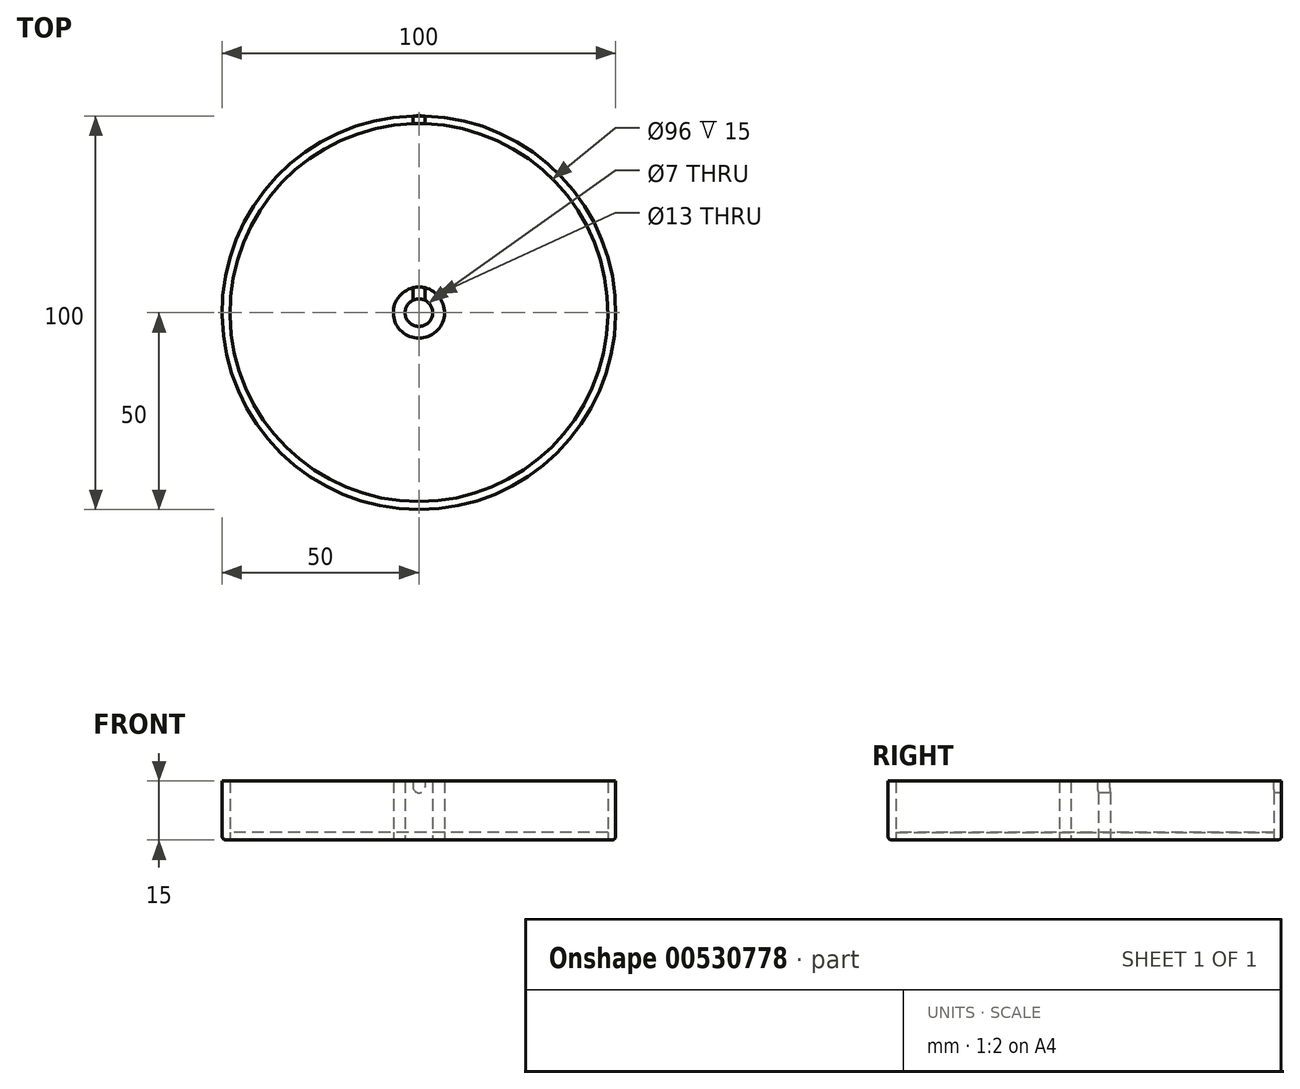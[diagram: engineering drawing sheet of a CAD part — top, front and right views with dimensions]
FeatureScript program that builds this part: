
annotation { "Feature Type Name" : "Feature", "Feature Type Description" : "" }
export const myFeature = defineFeature(function(context is Context, id is Id, definition is map)
    precondition{}
    {
        {
            var Q0;
            Q0=qCreatedBy(makeId("Top.planeOp"),FACE);
            var sketch = newSketch(context, id + "F0", { "sketchPlane" : qUnion([Q0])});
            skCircle(sketch, "E0", {"center": v(0, 0) * mm, "radius": 50 * mm});
            skCircle(sketch, "E1", {"center": v(0, 0) * mm, "radius": 48 * mm});
            skCircle(sketch, "E2", {"center": v(0, 0) * mm, "radius": 6.5 * mm});
            skCircle(sketch, "E3", {"center": v(0, 0) * mm, "radius": 3.5 * mm});
            skSolve(sketch);
        }
        {
            var Q0;
            Q0=makeQuery(id+"F0.imprint","IMPRINT",FACE,{"disambiguationData":[TD([[makeQuery(id+"F0.imprint","IMPRINT",EDGE,{"derivedFrom":sQuery(id+"F0.wireOp",EDGE,"E1")}),1.0]])]});
            extrude(context, id + "F1", {"entities" : qUnion([Q0]), "depth" : 2 * mm, "offsetDistance" : 25 * mm});
        }
        {
            var Q0;
            Q0=makeQuery(id+"F0.imprint","IMPRINT",FACE,{"disambiguationData":[TD([[makeQuery(id+"F0.imprint","IMPRINT",EDGE,{"derivedFrom":sQuery(id+"F0.wireOp",EDGE,"E2")}),1.0]])]});
            var Q1;
            Q1=makeQuery(id+"F0.imprint","IMPRINT",FACE,{"disambiguationData":[TD([[makeQuery(id+"F0.imprint","IMPRINT",EDGE,{"derivedFrom":sQuery(id+"F0.wireOp",EDGE,"E0")}),1.0]])]});
            extrude(context, id + "F2", {"entities" : qUnion([Q0, Q1]), "depth" : 15 * mm, "offsetDistance" : 25 * mm});
        }
        {
            var Q0;
            Q0=qCreatedBy(makeId("Front.planeOp"),FACE);
            var sketch = newSketch(context, id + "F3", { "sketchPlane" : qUnion([Q0])});
            skCircle(sketch, "E4", {"center": v(0, 13.5) * mm, "radius": 1.5 * mm});
            skLineSegment(sketch, "E5.bottom", {"start": v(1.5, 13.5) * mm, "end": v(-1.5, 13.5) * mm});
            skLineSegment(sketch, "E5.top", {"start": v(1.5, 16.5) * mm, "end": v(-1.5, 16.5) * mm});
            skLineSegment(sketch, "E5.left", {"start": v(1.5, 13.5) * mm, "end": v(1.5, 16.5) * mm});
            skLineSegment(sketch, "E5.right", {"start": v(-1.5, 13.5) * mm, "end": v(-1.5, 16.5) * mm});
            skSolve(sketch);
        }
        {
            var Q0;
            Q0=makeQuery(id+"F3.imprint","IMPRINT",FACE,{"disambiguationData":[TD([[makeQuery(id+"F3.imprint","IMPRINT",EDGE,{"derivedFrom":sQuery(id+"F3.wireOp",EDGE,"E5.top")}),1.0]])]});
            var Q1;
            {var subQ0=sQuery(id+"F3.wireOp",EDGE,"E5.bottom");Q1=makeQuery(id+"F3.imprint","IMPRINT",FACE,{"disambiguationData":[TD([[makeQuery(id+"F3.imprint","IMPRINT",EDGE,{"derivedFrom":subQ0}),-1.0]])]});}
            var Q2;
            {var subQ0=sQuery(id+"F3.wireOp",EDGE,"E5.bottom");Q2=makeQuery(id+"F3.imprint","IMPRINT",FACE,{"disambiguationData":[TD([[makeQuery(id+"F3.imprint","IMPRINT",EDGE,{"derivedFrom":subQ0}),1.0]])]});}
            extrude(context, id + "F4", {"entities" : qUnion([Q0, Q1, Q2]), "operationType" : NewBodyOperationType.REMOVE, "oppositeDirection" : true, "depth" : 70 * mm, "offsetDistance" : 25 * mm});
        }
        {
            var Q0;
            Q0=makeQuery(id+"F2.opExtrude","CAP_EDGE",EDGE,{"disambiguationData":[OSD([sQuery(id+"F0.wireOp",EDGE,"E0")])],"isStart":true});
            fillet(context, id + "F5", {"entities" : qUnion([Q0]), "radius" : 1 * mm, "tangentPropagation" : true, "allowEdgeOverflow" : false});
        }
    });
